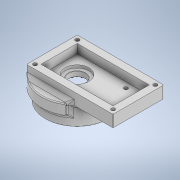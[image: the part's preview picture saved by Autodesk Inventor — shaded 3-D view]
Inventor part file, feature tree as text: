
AUTODESK INVENTOR PART (.ipt)
format: ipt  version: 2022 (Build 260153000, 153)  size: 799,744 bytes
history: native  units: mm
features: extrude x13, sketch x13, fillet x11, projected_geometry x3, other x2, pattern_circular x1
ambient origin geometry x8: Origin, YZ Plane, XZ Plane, XY Plane, X Axis, Y Axis, Z Axis, Center Point
bodies: Body1 (feature_tree)
feature tree (43):
  other  "Твердое тело1"
  extrude  "Выдавливание1"  Depth=20.0mm
  extrude  "Выдавливание3"  Depth=39.7mm
  extrude  "Выдавливание4"  Depth=4.0mm
  extrude  "Выдавливание6"  Depth=4.0mm
  extrude  "Выдавливание8"  Depth=5.0mm TaperAngle=0.0deg
  extrude  "Выдавливание9"  Depth=13.2mm
  fillet  "Сопряжение1"  Radius=9.8mm
  extrude  "Выдавливание10"  Depth=16.6mm
  extrude  "Выдавливание12"  Depth=8.0mm
  fillet  "Сопряжение4"  Radius=2.1mm
  extrude  "Выдавливание13"  Depth=13.22mm
  fillet  "Сопряжение5"  Radius=7.0mm
  fillet  "Сопряжение6"  Radius=7.0mm
  fillet  "Сопряжение7"  Radius=1.5mm
  extrude  "Выдавливание15"  Depth=2.1mm
  fillet  "Сопряжение8"  Radius=100.0mm
  other  "РабОсь1"
  pattern_circular  "Круговой массив1"  [2 undecoded]
  fillet  "Сопряжение9"  Radius=35.0mm
  fillet  "Сопряжение11"  Radius=2.9mm
  fillet  "Сопряжение12"  Radius=20.0mm
  fillet  "Сопряжение13"  Radius=2.1mm
  extrude  "Выдавливание16"  Depth=2.0mm
  extrude  "Выдавливание17"  Depth=6.0mm TaperAngle=0.0deg
  extrude  "Выдавливание18"  Depth=2.0mm
  fillet  "Сопряжение15"  Radius=4.0mm
  sketch  "Эскиз1"
  sketch  "Эскиз2"
  sketch  "Эскиз3"
  projected_geometry  "Спроецированная петля1"
  sketch  "Эскиз4"
  projected_geometry  "Спроецированная петля2"
  sketch  "Эскиз6"
  projected_geometry  "Спроецированная петля3"
  sketch  "Эскиз7"
  sketch  "Эскиз8"
  sketch  "Эскиз9"
  sketch  "Эскиз10"
  sketch  "Эскиз12"
  sketch  "Эскиз13"
  sketch  "Эскиз14"
  sketch  "Эскиз15"
note: 2 required parameter values undecoded (feature->parameter linkage not recoverable at this tier; creation-order binding heuristic only, values carry confidence <= 0.55)
